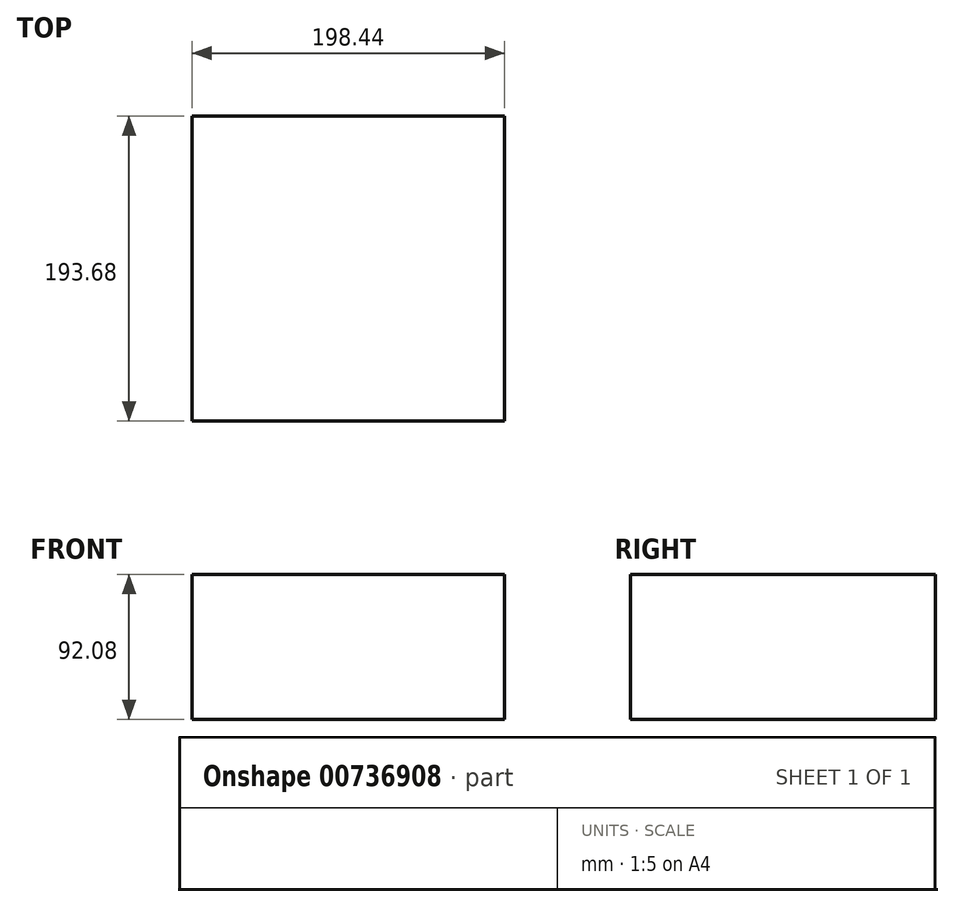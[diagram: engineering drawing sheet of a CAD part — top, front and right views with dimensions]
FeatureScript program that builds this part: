
annotation { "Feature Type Name" : "Feature", "Feature Type Description" : "" }
export const myFeature = defineFeature(function(context is Context, id is Id, definition is map)
    precondition{}
    {
        {
            var Q0;
            Q0=qCreatedBy(makeId("Top.planeOp"),FACE);
            var sketch = newSketch(context, id + "F0", { "sketchPlane" : qUnion([Q0])});
            skLineSegment(sketch, "E0.bottom", {"start": v(0, 0) * mm, "end": v(198.44, 0) * mm});
            skLineSegment(sketch, "E0.top", {"start": v(0, 193.68) * mm, "end": v(198.44, 193.68) * mm});
            skLineSegment(sketch, "E0.left", {"start": v(0, 0) * mm, "end": v(0, 193.68) * mm});
            skLineSegment(sketch, "E0.right", {"start": v(198.44, 0) * mm, "end": v(198.44, 193.68) * mm});
            skSolve(sketch);
        }
        {
            var Q0;
            Q0=makeQuery(id+"F0.imprint","IMPRINT",FACE,{"disambiguationData":[TD([[makeQuery(id+"F0.imprint","IMPRINT",EDGE,{"derivedFrom":sQuery(id+"F0.wireOp",EDGE,"E0.bottom")}),1.0]])]});
            extrude(context, id + "F1", {"entities" : qUnion([Q0]), "depth" : 92.07 * mm, "offsetDistance" : 25.4 * mm});
        }
    });
